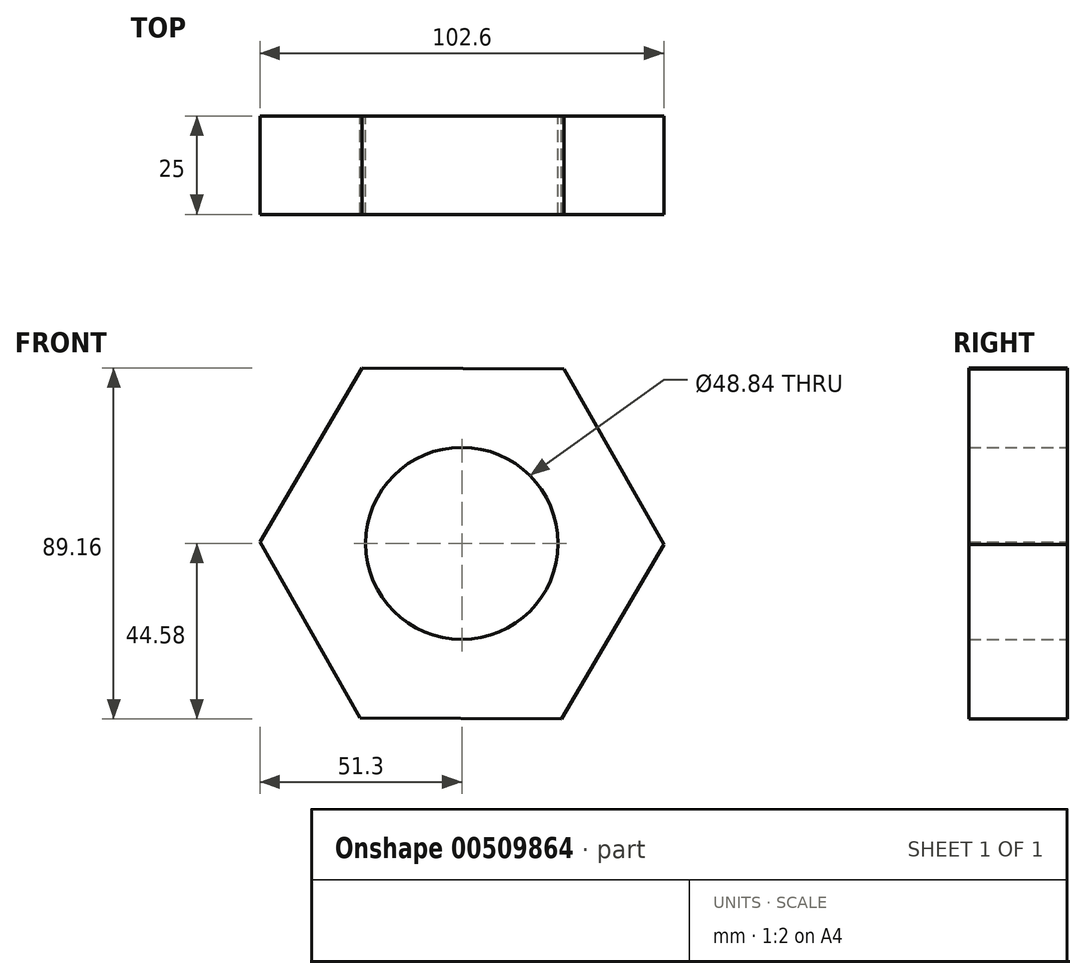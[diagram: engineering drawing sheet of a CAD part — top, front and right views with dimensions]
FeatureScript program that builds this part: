
annotation { "Feature Type Name" : "Feature", "Feature Type Description" : "" }
export const myFeature = defineFeature(function(context is Context, id is Id, definition is map)
    precondition{}
    {
        {
            var Q0;
            Q0=qCreatedBy(makeId("Front.planeOp"),FACE);
            var sketch = newSketch(context, id + "F0", { "sketchPlane" : qUnion([Q0])});
            skCircle(sketch, "E0.cCircle", {"center": v(0, 0) * mm, "radius": 44.43 * mm, "construction": true});
            skLineSegment(sketch, "E0.0", {"start": v(-25.92, -44.27) * mm, "end": v(-51.3, 0.31) * mm});
            skLineSegment(sketch, "E0.1", {"start": v(-51.3, 0.31) * mm, "end": v(-25.38, 44.58) * mm});
            skLineSegment(sketch, "E0.2", {"start": v(-25.38, 44.58) * mm, "end": v(25.92, 44.27) * mm});
            skLineSegment(sketch, "E0.3", {"start": v(25.92, 44.27) * mm, "end": v(51.3, -0.31) * mm});
            skLineSegment(sketch, "E0.4", {"start": v(51.3, -0.31) * mm, "end": v(25.38, -44.58) * mm});
            skLineSegment(sketch, "E0.5", {"start": v(25.38, -44.58) * mm, "end": v(-25.92, -44.27) * mm});
            skPoint(sketch, "E0.0.midPoint", {"position": v(-38.61, -21.98) * mm});
            skCircle(sketch, "E1", {"center": v(0, 0) * mm, "radius": 24.42 * mm});
            skSolve(sketch);
        }
        {
            var Q0;
            Q0 = qSketchRegion(id + "F0", true);
            extrude(context, id + "F1", {"entities" : qUnion([Q0]), "depth" : 25 * mm, "offsetDistance" : 25 * mm});
        }
    });
